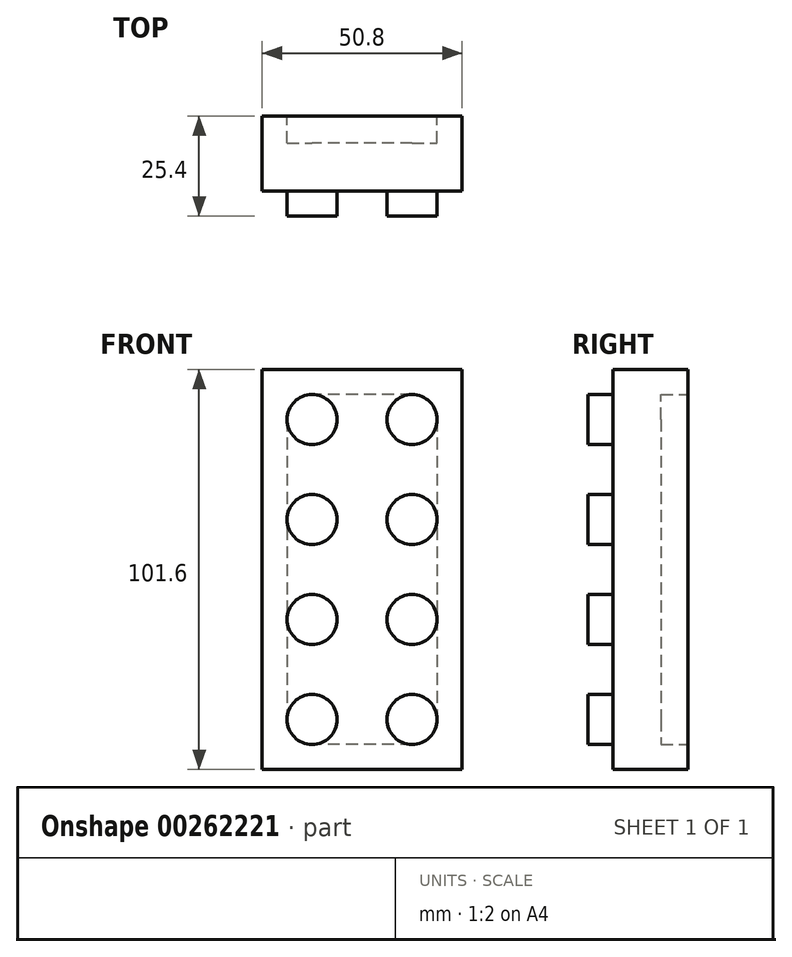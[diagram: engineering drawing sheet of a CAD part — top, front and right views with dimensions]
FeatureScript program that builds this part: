
annotation { "Feature Type Name" : "Feature", "Feature Type Description" : "" }
export const myFeature = defineFeature(function(context is Context, id is Id, definition is map)
    precondition{}
    {
        {
            var Q0;
            Q0=qCreatedBy(makeId("Front.planeOp"),FACE);
            var sketch = newSketch(context, id + "F0", { "sketchPlane" : qUnion([Q0])});
            skLineSegment(sketch, "E0.bottom", {"start": v(0, 0) * mm, "end": v(50.8, 0) * mm});
            skLineSegment(sketch, "E0.top", {"start": v(0, 101.6) * mm, "end": v(50.8, 101.6) * mm});
            skLineSegment(sketch, "E0.left", {"start": v(0, 0) * mm, "end": v(0, 101.6) * mm});
            skLineSegment(sketch, "E0.right", {"start": v(50.8, 0) * mm, "end": v(50.8, 101.6) * mm});
            skSolve(sketch);
        }
        {
            var Q0;
            Q0 = qSketchRegion(id + "F0", true);
            extrude(context, id + "F1", {"entities" : qUnion([Q0]), "depth" : 19.05 * mm});
        }
        {
            var Q0;
            Q0=makeQuery(id+"F1.opExtrude","CAP_FACE",FACE,{"disambiguationData":[OSD([sQuery(id+"F0.wireOp",EDGE,"E0.bottom"),sQuery(id+"F0.wireOp",EDGE,"E0.top"),sQuery(id+"F0.wireOp",EDGE,"E0.left"),sQuery(id+"F0.wireOp",EDGE,"E0.right")])],"isStart":false});
            var sketch = newSketch(context, id + "F2", { "sketchPlane" : qUnion([Q0])});
            skCircle(sketch, "E1", {"center": v(12.7, 88.9) * mm, "radius": 6.35 * mm});
            skCircle(sketch, "E2", {"center": v(38.1, 88.9) * mm, "radius": 6.35 * mm});
            skCircle(sketch, "E3", {"center": v(12.7, 63.5) * mm, "radius": 6.35 * mm});
            skCircle(sketch, "E4", {"center": v(38.1, 63.5) * mm, "radius": 6.35 * mm});
            skCircle(sketch, "E5", {"center": v(12.7, 38.1) * mm, "radius": 6.35 * mm});
            skCircle(sketch, "E6", {"center": v(38.1, 38.1) * mm, "radius": 6.35 * mm});
            skCircle(sketch, "E7", {"center": v(12.7, 12.7) * mm, "radius": 6.35 * mm});
            skCircle(sketch, "E8", {"center": v(38.1, 12.7) * mm, "radius": 6.35 * mm});
            skSolve(sketch);
        }
        {
            var Q0;
            Q0 = qSketchRegion(id + "F2", true);
            extrude(context, id + "F3", {"entities" : qUnion([Q0]), "operationType" : NewBodyOperationType.ADD, "depth" : 6.35 * mm});
        }
        {
            var Q0;
            Q0=makeQuery(id+"F1.opExtrude","CAP_FACE",FACE,{"disambiguationData":[OSD([sQuery(id+"F0.wireOp",EDGE,"E0.bottom"),sQuery(id+"F0.wireOp",EDGE,"E0.top"),sQuery(id+"F0.wireOp",EDGE,"E0.left"),sQuery(id+"F0.wireOp",EDGE,"E0.right")])],"isStart":true});
            var sketch = newSketch(context, id + "F4", { "sketchPlane" : qUnion([Q0])});
            skLineSegment(sketch, "E9.bottom", {"start": v(-38.1, 95.25) * mm, "end": v(-12.7, 95.25) * mm});
            skLineSegment(sketch, "E9.top", {"start": v(-38.1, 6.35) * mm, "end": v(-12.7, 6.35) * mm});
            skLineSegment(sketch, "E9.left", {"start": v(-44.45, 88.9) * mm, "end": v(-44.45, 12.7) * mm});
            skLineSegment(sketch, "E9.right", {"start": v(-6.35, 88.9) * mm, "end": v(-6.35, 12.7) * mm});
            skPoint(sketch, "E10.visualSharp", {"position": v(-44.45, 95.25) * mm});
            skArc(sketch, "E10.filletArc", {"start": v(-38.1, 95.25) * mm, "mid": v(-42.6, 93.4) * mm, "end": v(-44.45, 88.9) * mm});
            skPoint(sketch, "E11.visualSharp", {"position": v(-6.35, 95.25) * mm});
            skArc(sketch, "E11.filletArc", {"start": v(-6.35, 88.9) * mm, "mid": v(-8.2, 93.4) * mm, "end": v(-12.7, 95.25) * mm});
            skPoint(sketch, "E12.visualSharp", {"position": v(-6.35, 6.35) * mm});
            skArc(sketch, "E12.filletArc", {"start": v(-12.7, 6.35) * mm, "mid": v(-8.2, 8.2) * mm, "end": v(-6.35, 12.7) * mm});
            skPoint(sketch, "E13.visualSharp", {"position": v(-44.45, 6.35) * mm});
            skArc(sketch, "E13.filletArc", {"start": v(-44.45, 12.7) * mm, "mid": v(-42.6, 8.2) * mm, "end": v(-38.1, 6.35) * mm});
            skSolve(sketch);
        }
        {
            var Q0;
            Q0 = qSketchRegion(id + "F4", true);
            extrude(context, id + "F5", {"entities" : qUnion([Q0]), "operationType" : NewBodyOperationType.REMOVE, "oppositeDirection" : true, "depth" : 6.86 * mm});
        }
    });
